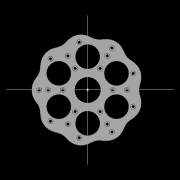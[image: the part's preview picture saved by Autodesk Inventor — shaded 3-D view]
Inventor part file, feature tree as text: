
AUTODESK INVENTOR PART (.ipt)
format: ipt  version: 2022.2 (Build 262287010, 287A)  size: 826,368 bytes
history: native  units: mm
features: other x20, extrude x17, sketch x12, pattern_circular x7, plane x4, fillet x2, move_body x2, revolve x2, draft x2, chamfer x2
ambient origin geometry x8: Origin, YZ Plane, XZ Plane, XY Plane, X Axis, Y Axis, Z Axis, Center Point
bodies: Solid5 (feature_tree)
feature tree (70):
  other  "CrossSection1"
  sketch  "Sketch7"  dims[d90=15.767323mm]
  other  "Roller1"
  other  "Roller2"
  sketch  "Sketch22"  dims[d167=8.972256mm]
  sketch  "Sketch2"  dims[d57=4.025mm]
  sketch  "Sketch23"  dims[d173=10.814812mm]
  other  "RevRoller1"
  fillet  "Fillet1"  Radius=13.336791mm
  pattern_circular  "Circular Pattern13"  Count=360  [1 undecoded]
  move_body  "Move Body7"
  revolve  "Revolution13"  [1 undecoded]
  fillet  "Fillet3"  Radius=0.025mm
  pattern_circular  "Circular Pattern14"  [2 undecoded]
  move_body  "Move Body6"
  revolve  "Revolution14"  [1 undecoded]
  other  "OuterRim_Top2"
  other  "OuterRim_Bottom2"
  extrude  "Rotor_Ring"  Depth=1.0mm
  draft  "FaceDraft2"
  sketch  "Sketch30"  dims[d201=53.5mm d232=0.0mm d233=3600.0mm]
  plane  "Work Plane5"
  other  "Rotor Featurs"
  other  "RotorRim_Bottom"
  extrude  "Extrusion24"  Depth=1.0mm
  extrude  "Extrusion25"  Depth=1.0mm
  extrude  "Extrusion26"  TaperAngle=90.0deg  [1 undecoded]
  pattern_circular  "Circular Pattern23"  [2 undecoded]
  sketch  "Sketch41"  dims[d346=0.025mm]
  extrude  "Extrusion27"  Depth=1.0mm
  extrude  "Extrusion28"  TaperAngle=360.0deg  [1 undecoded]
  pattern_circular  "Circular Pattern24"  Angle=30.0deg  [1 undecoded]
  extrude  "Extrusion29"  Depth=1.0mm
  extrude  "Extrusion30"  Depth=1.0mm
  extrude  "Extrusion31"  Depth=1.0mm
  pattern_circular  "Circular Pattern25"  [2 undecoded]
  sketch  "Sketch42"  dims[d347=0.1mm]
  extrude  "Extrusion32"  TaperAngle=30.0deg  [1 undecoded]
  extrude  "Extrusion33"  TaperAngle=90.0deg  [1 undecoded]
  extrude  "Extrusion34"  Depth=1.0mm
  extrude  "Extrusion35"  Depth=1.0mm
  pattern_circular  "Circular Pattern26"  Angle=360.0deg  [1 undecoded]
  pattern_circular  "Circular Pattern27"  Angle=90.0deg  [1 undecoded]
  chamfer  "Chamfer1"  Distance=0.1mm
  chamfer  "Chamfer2"  Distance=0.025mm
  draft  "FaceDraft4"
  plane  "Work Plane7"
  sketch  "Sketch44"  dims[d349=17.374602mm]
  sketch  "Sketch45"  dims[d350=17.374329mm]
  extrude  "Extrusion39"  Depth=1.0mm
  extrude  "Extrusion40"  Depth=1.0mm
  plane  "Work Plane8"
  sketch  "Sketch46"  dims[d351=0.025mm d352=0.025mm d354=0.025mm d355=17.374329mm d356=17.374602mm d357=1.0mm d358=90.0deg d359=0.5mm d360=60.0mm d361=360.0deg d363=30.0deg d367=8.1mm d369=4.014775mm d370=0.025mm d371=1.0mm d372=30.0deg d373=90.0deg d374=0.5mm d375=60.0mm d376=360.0deg d378=90.0deg d379=0.1mm d380=0.025mm d381=0.025mm d382=0.025mm d383=0.025mm d384=10.461905mm d385=0.0mm d386=0.0mm d391=1.0mm d392=53.5mm d393=1.5mm d394=1.5mm d395=1.5mm d396=1.5mm d397=90.0deg d398=90.0deg d399=90.0deg d400=53.5mm d401=10.461905mm d402=0.0mm d486=0.436332mm d487=0.5mm d488=2.0mm d489=0.0mm d490=20.0mm d495=2.5mm d496=8.0mm d506=13.856406mm d507=55.5mm d508=8.0mm d509=0.05mm d510=2.5mm d511=30.0deg d512=12.0mm d513=6.0mm d514=0.2mm d515=30.0deg d516=131.0mm d517=65.5mm d518=0.2mm d519=100.0mm d520=120.0mm d521=2.0mm d522=150.0mm d530=50.0mm d531=5.5mm d532=5.5mm d533=5.5mm d534=87.0mm d535=73.5mm d536=55.0mm d537=27.0mm d538=3.0mm d539=2.4mm d540=0.0mm d541=0.0mm d542=0.0mm d543=5.5mm d544=3.0mm d545=0.0mm d546=90.0mm d547=360.0deg d549=3.0mm d550=3.0mm d551=2.4mm d552=0.0mm d553=5.230953mm d554=0.0mm d555=2.4mm d556=0.0mm d557=5.230953mm d558=0.0mm d559=5.230953mm d560=0.0mm d561=90.0mm d562=360.0deg d564=60.0mm d565=360.0deg d567=5.5mm d568=5.5mm d569=3.0mm d570=0.0mm d571=5.230953mm d572=0.0mm d573=3.0mm d574=0.0mm d575=5.230953mm d576=0.0mm d577=90.0mm d578=360.0deg d580=60.0mm d581=360.0deg d584=20.0mm d585=8.0mm d587=1.75mm d589=3.0mm d592=2.0mm d593=12.0mm d594=12.0mm d600=0.5mm d601=2.0mm d602=45.0deg d603=0.5mm d604=2.0mm d605=45.0deg d606=0.436332mm d607=0.5mm d608=0.0mm d609=20.0mm d611=360.0deg d613=0.0mm d614=0.0mm d615=50.0mm d617=1.0mm d618=3.0mm d619=20.0mm d621=360.0deg d623=0.8mm d624=0.0mm d625=0.8mm d626=0.0mm d627=20.0mm d635=12.0mm d640=2.5mm d641=100.0mm d643=360.0deg d645=0.0mm d646=3600.0mm d16=0.872665mm d17=0.872665mm d49=0.872665mm d50=0.872665mm d51=0.872665mm d52=0.872665mm d236=0.5mm d237=0.872665mm d238=0.5mm d239=0.872665mm d282=1.0mm d283=1.0mm d284=1.0mm d285=0.15mm d286=0.25mm d287=0.375mm d288=14.3117mm d289=0.75mm d290=20.594885mm d291=0.0625mm d292=0.75mm d293=0.375mm d405=0.5mm d406=0.872665mm d407=0.5mm d408=0.872665mm d413=0.5mm d414=0.872665mm d415=0.5mm d416=0.872665mm d417=0.5mm d418=0.872665mm d419=0.5mm d420=0.872665mm d421=0.872665mm d431=0.5mm d432=0.872665mm d433=0.5mm d434=0.872665mm d471=0.5mm d472=0.872665mm d473=0.5mm d474=0.872665mm d497=0.5mm d498=0.872665mm d499=0.5mm d500=0.872665mm d590=0.5mm d591=0.872665mm]
  plane  "Work Plane6"
  sketch  "Sketch43"  dims[d348=0.1mm]
  extrude  "Extrusion37"  Depth=1.0mm
  extrude  "Extrusion38"  Depth=1.0mm
  other  "2D Equation Curve1"
  sketch  "Sketch40"  dims[d343=17.374329mm d344=17.374602mm d345=0.025mm]
  other  "Work Axis6"
  other  "Work Axis7"
  other  "Work Axis8"
  other  "Work Axis9"
  other  "Work Axis10"
  other  "Work Point1"
  other  "Work Point2"
  other  "Work Point3"
  other  "Work Point4"
  other  "Work Point5"
  other  "2D Equation Curve2"
note: 16 required parameter values undecoded (feature->parameter linkage not recoverable at this tier; creation-order binding heuristic only, values carry confidence <= 0.55)